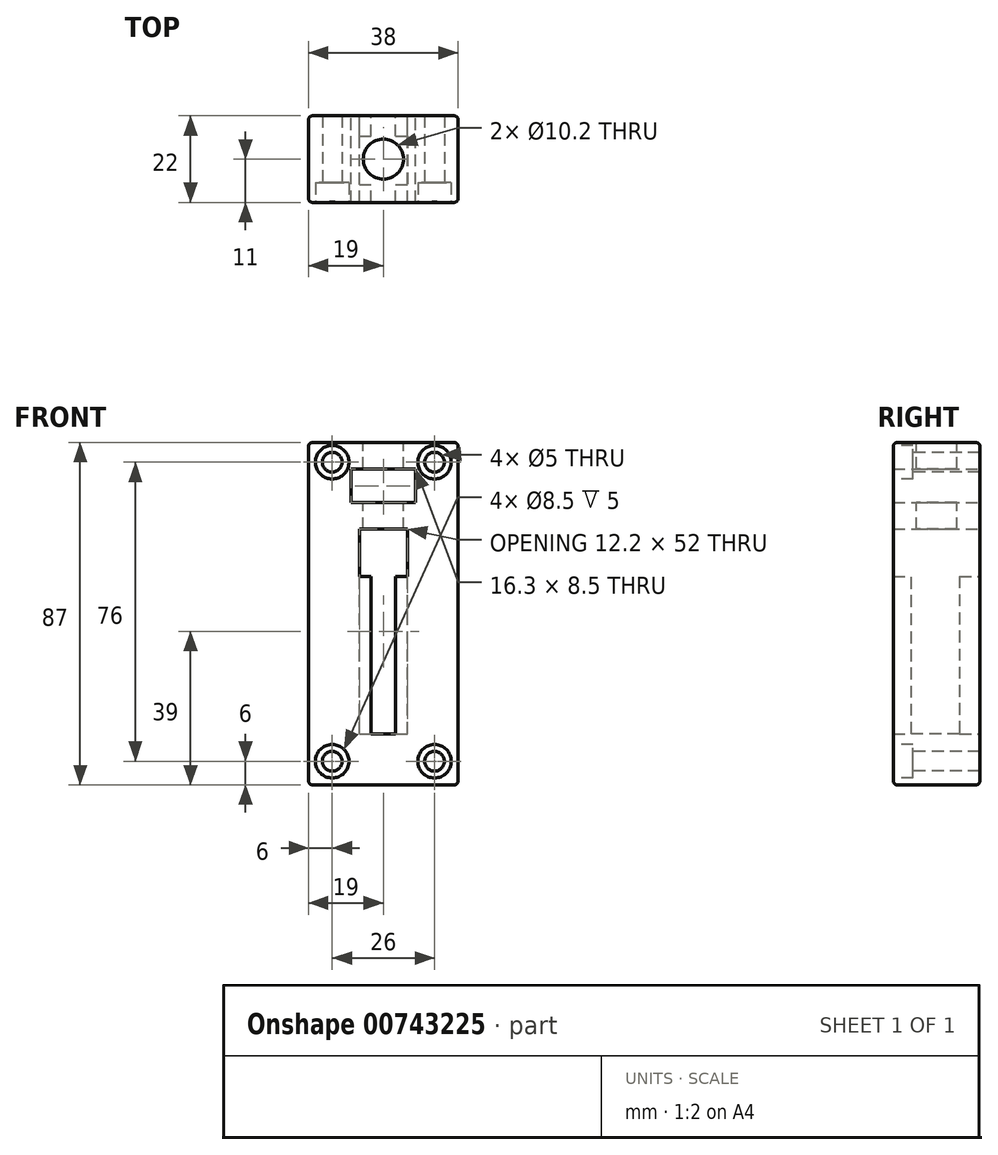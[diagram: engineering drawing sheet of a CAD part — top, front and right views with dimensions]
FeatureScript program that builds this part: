
annotation { "Feature Type Name" : "Feature", "Feature Type Description" : "" }
export const myFeature = defineFeature(function(context is Context, id is Id, definition is map)
    precondition{}
    {
        {
            var Q0;
            Q0=qCreatedBy(makeId("Front.planeOp"),FACE);
            var sketch = newSketch(context, id + "F0", { "sketchPlane" : qUnion([Q0])});
            skLineSegment(sketch, "E0.bottom", {"start": v(-3.1, 20) * mm, "end": v(3.1, 20) * mm});
            skLineSegment(sketch, "E0.top", {"start": v(-3.1, -20) * mm, "end": v(3.1, -20) * mm});
            skLineSegment(sketch, "E0.left", {"start": v(-3.1, 20) * mm, "end": v(-3.1, -20) * mm});
            skLineSegment(sketch, "E0.right", {"start": v(3.1, 20) * mm, "end": v(3.1, -20) * mm});
            skPoint(sketch, "E0.middle", {"position": v(0, 0) * mm});
            skLineSegment(sketch, "E1.bottom", {"start": v(-8.15, 38.75) * mm, "end": v(8.15, 38.75) * mm});
            skLineSegment(sketch, "E1.top", {"start": v(-8.15, 47.25) * mm, "end": v(8.15, 47.25) * mm});
            skLineSegment(sketch, "E1.left", {"start": v(-8.15, 38.75) * mm, "end": v(-8.15, 47.25) * mm});
            skLineSegment(sketch, "E1.right", {"start": v(8.15, 38.75) * mm, "end": v(8.15, 47.25) * mm});
            skPoint(sketch, "E1.middle", {"position": v(0, 43) * mm});
            skLineSegment(sketch, "E2.bottom", {"start": v(-19, 54) * mm, "end": v(19, 54) * mm});
            skLineSegment(sketch, "E2.top", {"start": v(-19, 32) * mm, "end": v(19, 32) * mm});
            skLineSegment(sketch, "E2.left", {"start": v(-19, 54) * mm, "end": v(-19, 32) * mm});
            skLineSegment(sketch, "E2.right", {"start": v(19, 54) * mm, "end": v(19, 32) * mm});
            skLineSegment(sketch, "E3.bottom", {"start": v(19, 32) * mm, "end": v(-19, 32) * mm});
            skLineSegment(sketch, "E3.top", {"start": v(19, -33) * mm, "end": v(-19, -33) * mm});
            skLineSegment(sketch, "E3.left", {"start": v(19, 32) * mm, "end": v(19, -33) * mm});
            skLineSegment(sketch, "E3.right", {"start": v(-19, 32) * mm, "end": v(-19, -33) * mm});
            skLineSegment(sketch, "E4.bottom", {"start": v(6.1, 32) * mm, "end": v(-6.1, 32) * mm});
            skLineSegment(sketch, "E4.top", {"start": v(6.1, 20) * mm, "end": v(-6.1, 20) * mm});
            skLineSegment(sketch, "E4.left", {"start": v(6.1, 32) * mm, "end": v(6.1, 20) * mm});
            skLineSegment(sketch, "E4.right", {"start": v(-6.1, 32) * mm, "end": v(-6.1, 20) * mm});
            skLineSegment(sketch, "E5", {"start": v(0, 66.47) * mm, "end": v(0, -39.97) * mm, "construction": true});
            skSolve(sketch);
        }
        {
            var Q0;
            Q0=makeQuery(id+"F0.imprint","IMPRINT",FACE,{"disambiguationData":[TD([[makeQuery(id+"F0.imprint","IMPRINT",EDGE,{"derivedFrom":sQuery(id+"F0.wireOp",EDGE,"E1.bottom")}),-1.0]])]});
            var Q1;
            Q1=makeQuery(id+"F0.imprint","IMPRINT",FACE,{"disambiguationData":[TD([[makeQuery(id+"F0.imprint","IMPRINT",EDGE,{"derivedFrom":sQuery(id+"F0.wireOp",EDGE,"E3.top")}),-1.0]])]});
            extrude(context, id + "F1", {"entities" : qUnion([Q0, Q1]), "depth" : 22 * mm, "offsetDistance" : 25 * mm});
        }
        {
            var Q0;
            Q0=makeQuery(id+"F1.opExtrude","SWEPT_FACE",FACE,{"disambiguationData":[OSD([sQuery(id+"F0.wireOp",EDGE,"E2.bottom")])]});
            var sketch = newSketch(context, id + "F2", { "sketchPlane" : qUnion([Q0])});
            skCircle(sketch, "E6", {"center": v(0, -11) * mm, "radius": 5.1 * mm});
            skPoint(sketch, "E6.centerSnap0", {"position": v(-19, -11) * mm});
            skSolve(sketch);
        }
        {
            var Q0;
            Q0=makeQuery(id+"F2.imprint","IMPRINT",FACE,{"disambiguationData":[TD([[makeQuery(id+"F2.imprint","IMPRINT",EDGE,{"derivedFrom":sQuery(id+"F2.wireOp",EDGE,"E6")}),1.0]])]});
            var Q1;
            Q1=makeQuery(id+"F1.opExtrude","SWEPT_FACE",FACE,{"disambiguationData":[OSD([sQuery(id+"F0.wireOp",EDGE,"E2.top")])]});
            extrude(context, id + "F3", {"entities" : qUnion([Q0]), "operationType" : NewBodyOperationType.REMOVE, "endBound" : BoundingType.UP_TO_SURFACE, "oppositeDirection" : true, "depth" : 25 * mm, "endBoundEntityFace" : qUnion([Q1]), "offsetDistance" : 25 * mm});
        }
        {
            var Q0;
            {var subQ0=sQuery(id+"F0.wireOp",EDGE,"E4.top");Q0=makeQuery(id+"F1.opExtrude","SWEPT_FACE",FACE,{"disambiguationData":[OSD([subQ0]),TDD([makeQuery(id+"F0.imprint","IMPRINT",EDGE,{"disambiguationData":[TD([[makeQuery(id+"F0.imprint","INTERSECT",VERTEX,{"derivedFrom":[sQuery(id+"F0.wireOp",EDGE,"E0.left"),subQ0]}),-1.0]])],"derivedFrom":subQ0})])]});}
            var sketch = newSketch(context, id + "F4", { "sketchPlane" : qUnion([Q0])});
            skLineSegment(sketch, "E7.bottom", {"start": v(-6.1, -5.22) * mm, "end": v(6.1, -5.22) * mm});
            skLineSegment(sketch, "E7.top", {"start": v(-6.1, -17.42) * mm, "end": v(6.1, -17.42) * mm});
            skLineSegment(sketch, "E7.left", {"start": v(-6.1, -5.22) * mm, "end": v(-6.1, -17.42) * mm});
            skLineSegment(sketch, "E7.right", {"start": v(6.1, -5.22) * mm, "end": v(6.1, -17.42) * mm});
            skPoint(sketch, "E7.middle", {"position": v(0, -11.32) * mm});
            skSolve(sketch);
        }
        {
            var Q0;
            {var subQ0=sQuery(id+"F4.wireOp",EDGE,"E7.bottom");var subQ1=sQuery(id+"F0.wireOp",EDGE,"E4.top");var subQ2=makeQuery(id+"F1.opExtrude","SWEPT_EDGE",EDGE,{"disambiguationData":[OSD([subQ1,sQuery(id+"F0.wireOp",EDGE,"E4.right")])]});var subQ3=makeQuery(id+"F4.imprint","INTERSECT",VERTEX,{"derivedFrom":[subQ2,subQ0]});Q0=makeQuery(id+"F4.imprint","IMPRINT",FACE,{"disambiguationData":[TD([[makeQuery(id+"F4.imprint","IMPRINT",EDGE,{"disambiguationData":[TD([[subQ3,-1.0]])],"derivedFrom":subQ0}),-1.0]])]});}
            var Q1;
            {var subQ0=sQuery(id+"F4.wireOp",EDGE,"E7.right");Q1=makeQuery(id+"F4.imprint","IMPRINT",FACE,{"disambiguationData":[TD([[makeQuery(id+"F4.imprint","IMPRINT",EDGE,{"derivedFrom":subQ0}),-1.0]])]});}
            extrude(context, id + "F5", {"entities" : qUnion([Q0, Q1]), "operationType" : NewBodyOperationType.REMOVE, "oppositeDirection" : true, "depth" : 40 * mm, "offsetDistance" : 25 * mm});
        }
        {
            var Q0;
            Q0=makeQuery(id+"F1.opExtrude","CAP_FACE",FACE,{"disambiguationData":[OSD([sQuery(id+"F0.wireOp",EDGE,"E0.top"),sQuery(id+"F0.wireOp",EDGE,"E0.left"),sQuery(id+"F0.wireOp",EDGE,"E0.right"),sQuery(id+"F0.wireOp",EDGE,"E1.bottom"),sQuery(id+"F0.wireOp",EDGE,"E1.top"),sQuery(id+"F0.wireOp",EDGE,"E1.left"),sQuery(id+"F0.wireOp",EDGE,"E1.right"),sQuery(id+"F0.wireOp",EDGE,"E2.bottom"),sQuery(id+"F0.wireOp",EDGE,"E2.top"),sQuery(id+"F0.wireOp",EDGE,"E2.left"),sQuery(id+"F0.wireOp",EDGE,"E2.right"),sQuery(id+"F0.wireOp",EDGE,"E3.top"),sQuery(id+"F0.wireOp",EDGE,"E3.left"),sQuery(id+"F0.wireOp",EDGE,"E3.right"),sQuery(id+"F0.wireOp",EDGE,"E4.top"),sQuery(id+"F0.wireOp",EDGE,"E4.left"),sQuery(id+"F0.wireOp",EDGE,"E4.right")])],"isStart":false});
            var sketch = newSketch(context, id + "F6", { "sketchPlane" : qUnion([Q0])});
            skLineSegment(sketch, "E8.bottom", {"start": v(-13, 49) * mm, "end": v(13, 49) * mm, "construction": true});
            skLineSegment(sketch, "E8.top", {"start": v(-13, -27) * mm, "end": v(13, -27) * mm, "construction": true});
            skLineSegment(sketch, "E8.left", {"start": v(-13, 49) * mm, "end": v(-13, -27) * mm, "construction": true});
            skLineSegment(sketch, "E8.right", {"start": v(13, 49) * mm, "end": v(13, -27) * mm, "construction": true});
            skPoint(sketch, "E8.middle", {"position": v(0, 11) * mm});
            skCircle(sketch, "E9", {"center": v(13, 49) * mm, "radius": 2.5 * mm});
            skCircle(sketch, "E10", {"center": v(-13, 49) * mm, "radius": 2.5 * mm});
            skCircle(sketch, "E11", {"center": v(-13, -27) * mm, "radius": 2.5 * mm});
            skCircle(sketch, "E12", {"center": v(13, -27) * mm, "radius": 2.5 * mm});
            skCircle(sketch, "E13", {"center": v(-13, 49) * mm, "radius": 4.25 * mm});
            skCircle(sketch, "E14", {"center": v(13, 49) * mm, "radius": 4.25 * mm});
            skCircle(sketch, "E15", {"center": v(13, -27) * mm, "radius": 4.25 * mm});
            skCircle(sketch, "E16", {"center": v(-13, -27) * mm, "radius": 4.25 * mm});
            skSolve(sketch);
        }
        {
            var Q0;
            Q0=makeQuery(id+"F6.imprint","IMPRINT",FACE,{"disambiguationData":[TD([[makeQuery(id+"F6.imprint","IMPRINT",EDGE,{"derivedFrom":sQuery(id+"F6.wireOp",EDGE,"E10")}),1.0]])]});
            var Q1;
            Q1=makeQuery(id+"F6.imprint","IMPRINT",FACE,{"disambiguationData":[TD([[makeQuery(id+"F6.imprint","IMPRINT",EDGE,{"derivedFrom":sQuery(id+"F6.wireOp",EDGE,"E9")}),1.0]])]});
            var Q2;
            Q2=makeQuery(id+"F6.imprint","IMPRINT",FACE,{"disambiguationData":[TD([[makeQuery(id+"F6.imprint","IMPRINT",EDGE,{"derivedFrom":sQuery(id+"F6.wireOp",EDGE,"E11")}),1.0]])]});
            var Q3;
            Q3=makeQuery(id+"F6.imprint","IMPRINT",FACE,{"disambiguationData":[TD([[makeQuery(id+"F6.imprint","IMPRINT",EDGE,{"derivedFrom":sQuery(id+"F6.wireOp",EDGE,"E12")}),1.0]])]});
            extrude(context, id + "F7", {"entities" : qUnion([Q0, Q1, Q2, Q3]), "operationType" : NewBodyOperationType.REMOVE, "endBound" : BoundingType.THROUGH_ALL, "oppositeDirection" : true, "depth" : 25 * mm, "offsetDistance" : 25 * mm});
        }
        {
            var Q0;
            Q0=makeQuery(id+"F6.imprint","IMPRINT",FACE,{"disambiguationData":[TD([[makeQuery(id+"F6.imprint","IMPRINT",EDGE,{"derivedFrom":sQuery(id+"F6.wireOp",EDGE,"E10")}),-1.0]])]});
            var Q1;
            Q1=makeQuery(id+"F6.imprint","IMPRINT",FACE,{"disambiguationData":[TD([[makeQuery(id+"F6.imprint","IMPRINT",EDGE,{"derivedFrom":sQuery(id+"F6.wireOp",EDGE,"E9")}),-1.0]])]});
            var Q2;
            Q2=makeQuery(id+"F6.imprint","IMPRINT",FACE,{"disambiguationData":[TD([[makeQuery(id+"F6.imprint","IMPRINT",EDGE,{"derivedFrom":sQuery(id+"F6.wireOp",EDGE,"E12")}),-1.0]])]});
            var Q3;
            Q3=makeQuery(id+"F6.imprint","IMPRINT",FACE,{"disambiguationData":[TD([[makeQuery(id+"F6.imprint","IMPRINT",EDGE,{"derivedFrom":sQuery(id+"F6.wireOp",EDGE,"E11")}),-1.0]])]});
            extrude(context, id + "F8", {"entities" : qUnion([Q0, Q1, Q2, Q3]), "operationType" : NewBodyOperationType.REMOVE, "oppositeDirection" : true, "depth" : 5 * mm, "offsetDistance" : 25 * mm});
        }
        {
            var Q0;
            Q0=makeQuery(id+"F1.opExtrude","CAP_EDGE",EDGE,{"disambiguationData":[OSD([sQuery(id+"F0.wireOp",EDGE,"E2.right"),sQuery(id+"F0.wireOp",EDGE,"E3.left")])],"isStart":false});
            var Q1;
            Q1=makeQuery(id+"F1.opExtrude","CAP_EDGE",EDGE,{"disambiguationData":[OSD([sQuery(id+"F0.wireOp",EDGE,"E2.bottom")])],"isStart":false});
            var Q2;
            Q2=makeQuery(id+"F1.opExtrude","CAP_EDGE",EDGE,{"disambiguationData":[OSD([sQuery(id+"F0.wireOp",EDGE,"E2.left"),sQuery(id+"F0.wireOp",EDGE,"E3.right")])],"isStart":false});
            var Q3;
            Q3=makeQuery(id+"F1.opExtrude","CAP_EDGE",EDGE,{"disambiguationData":[OSD([sQuery(id+"F0.wireOp",EDGE,"E3.top")])],"isStart":false});
            var Q4;
            Q4=makeQuery(id+"F1.opExtrude","SWEPT_EDGE",EDGE,{"disambiguationData":[OSD([sQuery(id+"F0.wireOp",EDGE,"E3.top"),sQuery(id+"F0.wireOp",EDGE,"E3.left")])]});
            var Q5;
            Q5=makeQuery(id+"F1.opExtrude","SWEPT_EDGE",EDGE,{"disambiguationData":[OSD([sQuery(id+"F0.wireOp",EDGE,"E2.bottom"),sQuery(id+"F0.wireOp",EDGE,"E2.right")])]});
            var Q6;
            Q6=makeQuery(id+"F1.opExtrude","SWEPT_EDGE",EDGE,{"disambiguationData":[OSD([sQuery(id+"F0.wireOp",EDGE,"E2.bottom"),sQuery(id+"F0.wireOp",EDGE,"E2.left")])]});
            var Q7;
            Q7=makeQuery(id+"F1.opExtrude","CAP_EDGE",EDGE,{"disambiguationData":[OSD([sQuery(id+"F0.wireOp",EDGE,"E2.bottom")])],"isStart":true});
            var Q8;
            Q8=makeQuery(id+"F1.opExtrude","CAP_EDGE",EDGE,{"disambiguationData":[OSD([sQuery(id+"F0.wireOp",EDGE,"E2.left"),sQuery(id+"F0.wireOp",EDGE,"E3.right")])],"isStart":true});
            var Q9;
            Q9=makeQuery(id+"F1.opExtrude","SWEPT_EDGE",EDGE,{"disambiguationData":[OSD([sQuery(id+"F0.wireOp",EDGE,"E3.top"),sQuery(id+"F0.wireOp",EDGE,"E3.right")])]});
            var Q10;
            Q10=makeQuery(id+"F1.opExtrude","CAP_EDGE",EDGE,{"disambiguationData":[OSD([sQuery(id+"F0.wireOp",EDGE,"E3.top")])],"isStart":true});
            var Q11;
            Q11=makeQuery(id+"F1.opExtrude","CAP_EDGE",EDGE,{"disambiguationData":[OSD([sQuery(id+"F0.wireOp",EDGE,"E2.right"),sQuery(id+"F0.wireOp",EDGE,"E3.left")])],"isStart":true});
            fillet(context, id + "F9", {"entities" : qUnion([Q0, Q1, Q2, Q3, Q4, Q5, Q6, Q7, Q8, Q9, Q10, Q11]), "tangentPropagation" : true, "radius" : 1 * mm, "defaultsChanged" : false, "vertexSettings" : [], "allowEdgeOverflow" : false});
        }
    });
